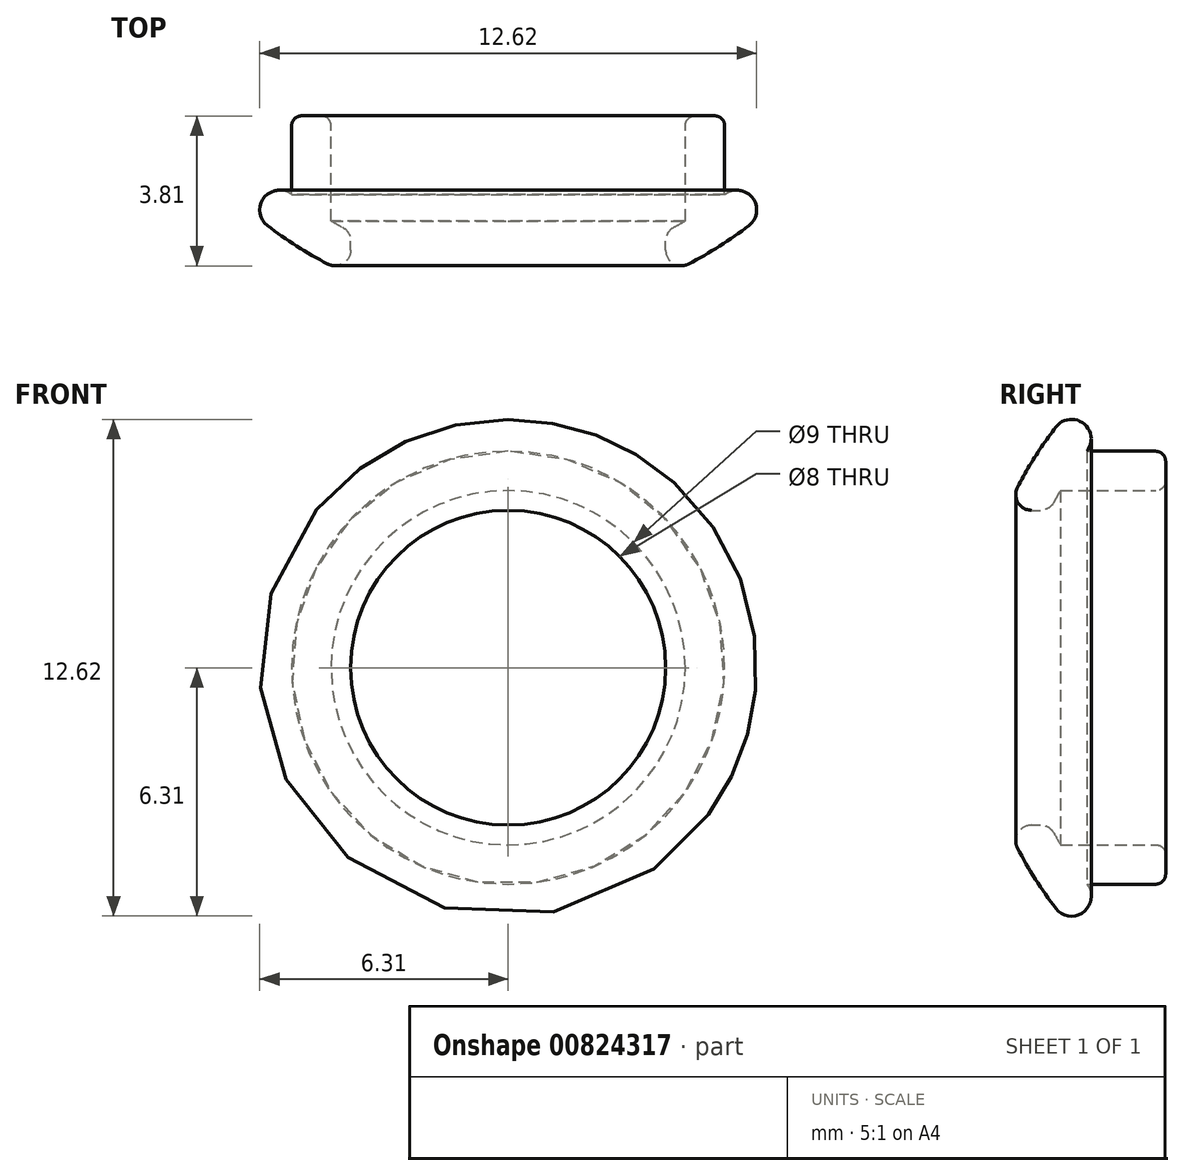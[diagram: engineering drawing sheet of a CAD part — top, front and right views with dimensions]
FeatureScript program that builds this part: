
annotation { "Feature Type Name" : "Feature", "Feature Type Description" : "" }
export const myFeature = defineFeature(function(context is Context, id is Id, definition is map)
    precondition{}
    {
        {
            var Q0;
            Q0=qCreatedBy(makeId("Right.planeOp"),FACE);
            var sketch = newSketch(context, id + "F0", { "sketchPlane" : qUnion([Q0])});
            skLineSegment(sketch, "E0", {"start": v(-29.19, -7.78) * mm, "end": v(-29.19, -7.78) * mm});
            skPoint(sketch, "E1.middle", {"position": v(0, 0) * mm});
            skLineSegment(sketch, "E2.top", {"start": v(-1.88, 4) * mm, "end": v(-1.65, 4) * mm});
            skArc(sketch, "E3", {"start": v(-1.25, 6.12) * mm, "mid": v(-1.78, 5.37) * mm, "end": v(-2.23, 4.58) * mm});
            skArc(sketch, "E4.0", {"start": v(-0.46, 5.5) * mm, "mid": v(-0.9, 4.88) * mm, "end": v(-1.3, 4.21) * mm});
            skLineSegment(sketch, "E5", {"start": v(-0.56, 6.21) * mm, "end": v(-0.56, 6.21) * mm});
            skPoint(sketch, "E6.visualSharp", {"position": v(-0.94, 6.5) * mm});
            skArc(sketch, "E6.filletArc", {"start": v(-0.56, 6.21) * mm, "mid": v(-0.93, 6.3) * mm, "end": v(-1.25, 6.12) * mm});
            skPoint(sketch, "E7.visualSharp", {"position": v(-0.14, 5.9) * mm});
            skArc(sketch, "E7.filletArc", {"start": v(-0.46, 5.5) * mm, "mid": v(-0.36, 5.88) * mm, "end": v(-0.56, 6.21) * mm});
            skLineSegment(sketch, "E8", {"start": v(1.28, 4.5) * mm, "end": v(-1.14, 4.5) * mm});
            skLineSegment(sketch, "E9.0", {"start": v(1.28, 5.5) * mm, "end": v(-0.47, 5.5) * mm});
            skLineSegment(sketch, "E10", {"start": v(1.53, 5.25) * mm, "end": v(1.53, 4.75) * mm});
            skPoint(sketch, "E11.visualSharp", {"position": v(1.53, 5.5) * mm});
            skArc(sketch, "E11.filletArc", {"start": v(1.53, 5.25) * mm, "mid": v(1.46, 5.43) * mm, "end": v(1.28, 5.5) * mm});
            skPoint(sketch, "E12.visualSharp", {"position": v(1.53, 4.5) * mm});
            skArc(sketch, "E12.filletArc", {"start": v(1.28, 4.5) * mm, "mid": v(1.46, 4.57) * mm, "end": v(1.53, 4.75) * mm});
            skArc(sketch, "E13.filletArc", {"start": v(-2.23, 4.58) * mm, "mid": v(-2.22, 4.2) * mm, "end": v(-1.88, 4) * mm});
            skArc(sketch, "E14.filletArc", {"start": v(-1.65, 4) * mm, "mid": v(-1.44, 4.06) * mm, "end": v(-1.3, 4.21) * mm});
            skLineSegment(sketch, "E15", {"start": v(0, 0) * mm, "end": v(-5.39, 0) * mm});
            skSolve(sketch);
        }
        {
            var Q0;
            Q0 = qSketchRegion(id + "F0", true);
            var Q1;
            Q1=sQuery(id+"F0.wireOp",EDGE,"E15");
            revolve(context, id + "F1", {"surfaceOperationType" : NewSurfaceOperationType.NEW, "entities" : qUnion([Q0]), "axis" : qUnion([Q1]), "revolveType" : RevolveType.FULL});
        }
    });
